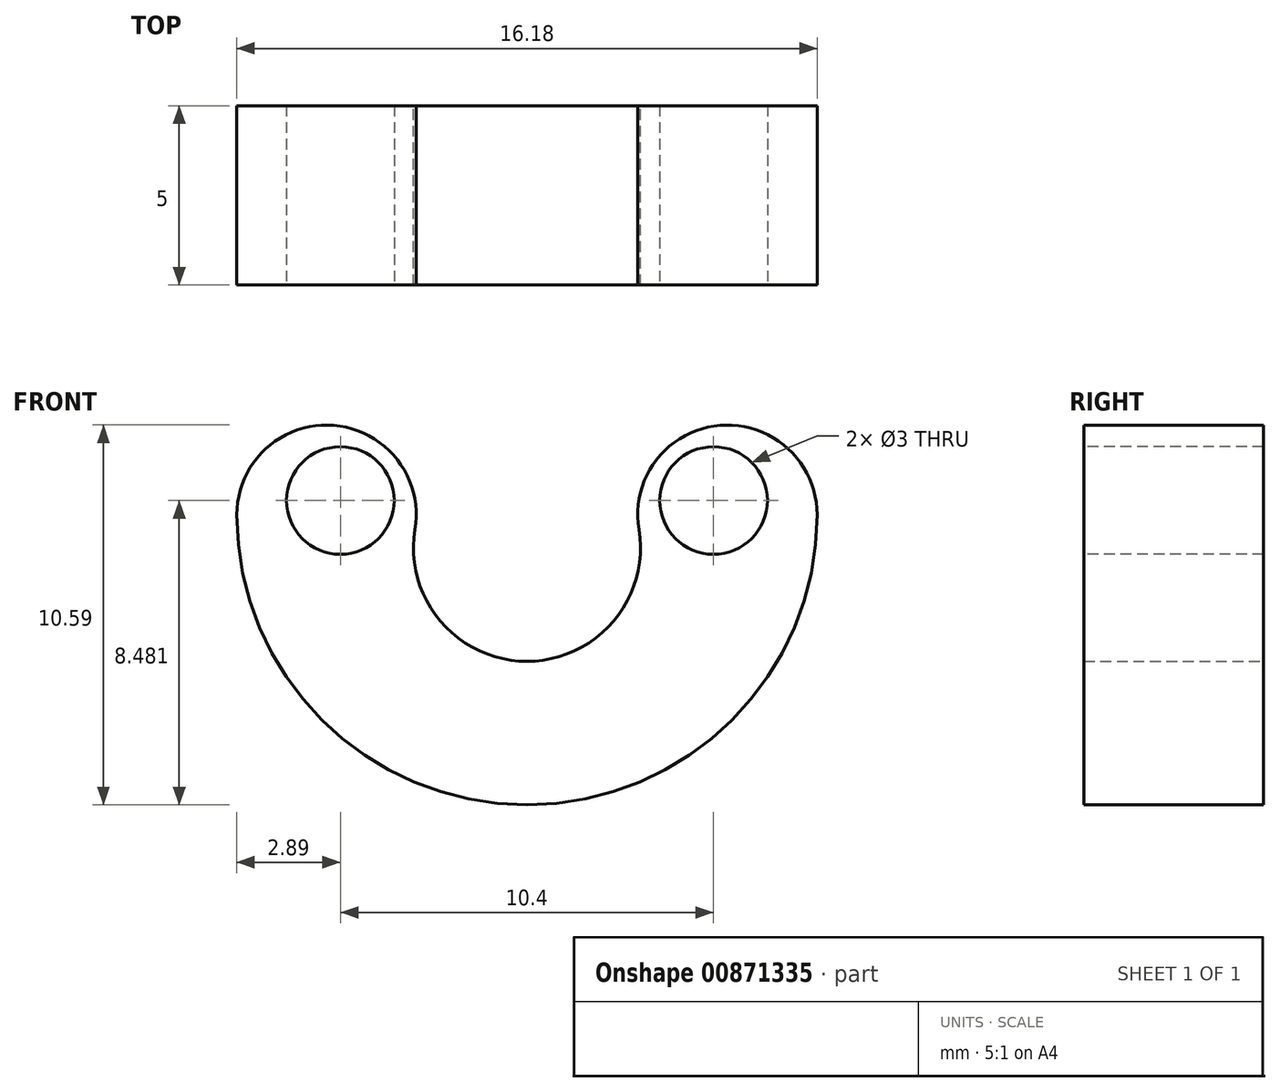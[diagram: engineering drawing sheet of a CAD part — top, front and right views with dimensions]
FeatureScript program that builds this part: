
annotation { "Feature Type Name" : "Feature", "Feature Type Description" : "" }
export const myFeature = defineFeature(function(context is Context, id is Id, definition is map)
    precondition{}
    {
        {
            var Q0;
            Q0=qCreatedBy(makeId("Front.planeOp"),FACE);
            var sketch = newSketch(context, id + "F0", { "sketchPlane" : qUnion([Q0])});
            skCircle(sketch, "E0", {"center": v(5.59, 8.09) * mm, "radius": 2.5 * mm});
            skCircle(sketch, "E1", {"center": v(-5.59, 8.09) * mm, "radius": 2.5 * mm});
            skArc(sketch, "E2", {"start": v(-8.09, 8.09) * mm, "mid": v(-5.72, 2.37) * mm, "end": v(0, 0) * mm});
            skArc(sketch, "E3.MirrorCS", {"start": v(8.09, 8.09) * mm, "mid": v(5.72, 2.37) * mm, "end": v(0, 0) * mm});
            skArc(sketch, "E4", {"start": v(-3.12, 7.68) * mm, "mid": v(0, 4) * mm, "end": v(3.12, 7.68) * mm});
            skSolve(sketch);
        }
        {
            var Q0;
            Q0 = qSketchRegion(id + "F0", true);
            extrude(context, id + "F1", {"entities" : qUnion([Q0]), "depth" : 5 * mm, "offsetDistance" : 25 * mm});
        }
        {
            var Q0;
            Q0=makeQuery(id+"F1.opExtrude","CAP_FACE",FACE,{"disambiguationData":[OSD([sQuery(id+"F0.wireOp",EDGE,"E0"),sQuery(id+"F0.wireOp",EDGE,"E1"),sQuery(id+"F0.wireOp",EDGE,"E2"),sQuery(id+"F0.wireOp",EDGE,"E3.MirrorCS"),sQuery(id+"F0.wireOp",EDGE,"gSvFGAoF-SGZH-NCw5-idr9-ttPFjwupo1L1")])],"isStart":false});
            var sketch = newSketch(context, id + "F2", { "sketchPlane" : qUnion([Q0])});
            skCircle(sketch, "E5", {"center": v(-5.2, 8.48) * mm, "radius": 1.5 * mm});
            skCircle(sketch, "E6", {"center": v(5.2, 8.48) * mm, "radius": 1.5 * mm});
            skSolve(sketch);
        }
        {
            var Q0;
            Q0 = qSketchRegion(id + "F2", true);
            extrude(context, id + "F3", {"entities" : qUnion([Q0]), "operationType" : NewBodyOperationType.REMOVE, "oppositeDirection" : true, "depth" : 25 * mm, "offsetDistance" : 25 * mm});
        }
    });
